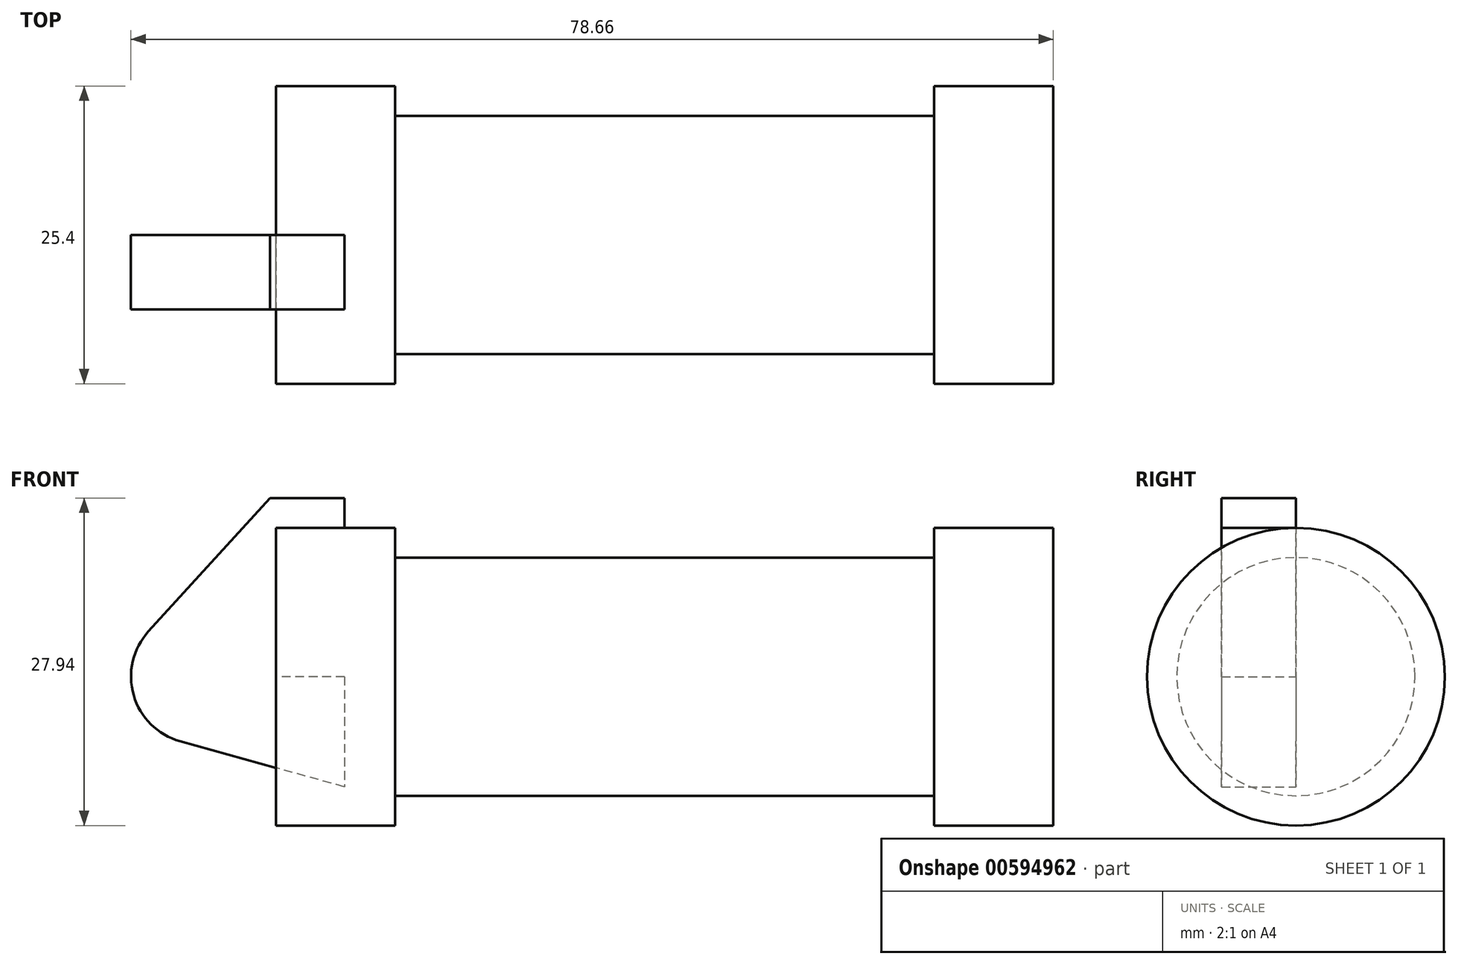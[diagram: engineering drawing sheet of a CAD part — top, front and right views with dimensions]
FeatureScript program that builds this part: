
annotation { "Feature Type Name" : "Feature", "Feature Type Description" : "" }
export const myFeature = defineFeature(function(context is Context, id is Id, definition is map)
    precondition{}
    {
        {
            var Q0;
            Q0=qCreatedBy(makeId("Front.planeOp"),FACE);
            var sketch = newSketch(context, id + "F0", { "sketchPlane" : qUnion([Q0])});
            skLineSegment(sketch, "E0", {"start": v(0, 0) * mm, "end": v(0, 12.7) * mm});
            skLineSegment(sketch, "E1", {"start": v(0, 12.7) * mm, "end": v(10.16, 12.7) * mm});
            skLineSegment(sketch, "E2", {"start": v(10.16, 12.7) * mm, "end": v(10.16, 10.16) * mm});
            skLineSegment(sketch, "E3", {"start": v(10.16, 10.16) * mm, "end": v(56.13, 10.16) * mm});
            skLineSegment(sketch, "E4", {"start": v(56.13, 10.16) * mm, "end": v(56.13, 12.7) * mm});
            skLineSegment(sketch, "E5", {"start": v(56.13, 12.7) * mm, "end": v(66.3, 12.7) * mm});
            skLineSegment(sketch, "E6", {"start": v(66.3, 12.7) * mm, "end": v(66.3, 0) * mm});
            skLineSegment(sketch, "E7", {"start": v(66.3, 0) * mm, "end": v(0, 0) * mm});
            skLineSegment(sketch, "E8", {"start": v(5.84, 15.24) * mm, "end": v(-0.5, 15.24) * mm});
            skLineSegment(sketch, "E9", {"start": v(-0.5, 15.24) * mm, "end": v(-10.88, 3.85) * mm});
            skLineSegment(sketch, "E10", {"start": v(0, 0) * mm, "end": v(-6.65, 0) * mm});
            skCircle(sketch, "E11", {"center": v(-6.65, 0) * mm, "radius": 5.72 * mm});
            skCircle(sketch, "E12", {"center": v(-6.65, 0) * mm, "radius": 3.18 * mm});
            skLineSegment(sketch, "E13", {"start": v(5.84, 15.24) * mm, "end": v(5.84, -9.4) * mm});
            skLineSegment(sketch, "E14", {"start": v(5.84, -9.4) * mm, "end": v(-8.18, -5.5) * mm});
            skSolve(sketch);
        }
        {
            var Q0;
            {var subQ0=sQuery(id+"F0.wireOp",EDGE,"E2");Q0=makeQuery(id+"F0.imprint","IMPRINT",FACE,{"disambiguationData":[TD([[makeQuery(id+"F0.imprint","IMPRINT",EDGE,{"derivedFrom":subQ0}),-1.0]])]});}
            var Q1;
            {var subQ0=sQuery(id+"F0.wireOp",EDGE,"E0");Q1=makeQuery(id+"F0.imprint","IMPRINT",FACE,{"disambiguationData":[TD([[makeQuery(id+"F0.imprint","IMPRINT",EDGE,{"derivedFrom":subQ0}),-1.0]])]});}
            var Q2;
            Q2=sQuery(id+"F0.wireOp",EDGE,"E7");
            revolve(context, id + "F1", {"entities" : qUnion([Q0, Q1]), "axis" : qUnion([Q2]), "revolveType" : RevolveType.FULL});
        }
        {
            var Q0;
            {var subQ1=sQuery(id+"F0.wireOp",EDGE,"E0");Q0=makeQuery(id+"F0.imprint","IMPRINT",FACE,{"disambiguationData":[TD([[makeQuery(id+"F0.imprint","IMPRINT",EDGE,{"derivedFrom":subQ1}),1.0]])]});}
            var Q1;
            {var subQ5=sQuery(id+"F0.wireOp",EDGE,"E12");Q1=makeQuery(id+"F0.imprint","IMPRINT",FACE,{"disambiguationData":[TD([[makeQuery(id+"F0.imprint","IMPRINT",EDGE,{"derivedFrom":subQ5}),-1.0]])]});}
            var Q2;
            {var subQ0=sQuery(id+"F0.wireOp",EDGE,"E12");Q2=makeQuery(id+"F0.imprint","IMPRINT",FACE,{"disambiguationData":[TD([[makeQuery(id+"F0.imprint","IMPRINT",EDGE,{"derivedFrom":subQ0}),1.0]])]});}
            var Q3;
            {var subQ0=sQuery(id+"F0.wireOp",EDGE,"E14");Q3=makeQuery(id+"F0.imprint","IMPRINT",FACE,{"disambiguationData":[TD([[makeQuery(id+"F0.imprint","IMPRINT",EDGE,{"derivedFrom":subQ0}),-1.0]])]});}
            extrude(context, id + "F2", {"entities" : qUnion([Q0, Q1, Q2, Q3]), "depth" : 6.35 * mm, "offsetDistance" : 25.4 * mm});
        }
        {
            var Q0;
            {var subQ0=sQuery(id+"F0.wireOp",EDGE,"E12");Q0=makeQuery(id+"F0.imprint","IMPRINT",FACE,{"disambiguationData":[TD([[makeQuery(id+"F0.imprint","IMPRINT",EDGE,{"derivedFrom":subQ0}),1.0]])]});}
            var Q1;
            Q1=sQuery(id+"F0.wireOp",EDGE,"E12");
            extrude(context, id + "F3", {"entities" : qUnion([Q0]), "operationType" : NewBodyOperationType.REMOVE, "surfaceEntities" : qUnion([Q1]), "endBound" : BoundingType.THROUGH_ALL, "oppositeDirection" : true, "depth" : 25.4 * mm, "offsetDistance" : 25.4 * mm});
        }
    });
